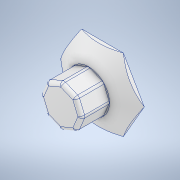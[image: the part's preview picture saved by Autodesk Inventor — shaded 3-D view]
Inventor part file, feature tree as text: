
AUTODESK INVENTOR PART (.ipt)
format: ipt  version: 2022 (Build 260153000, 153)  size: 275,456 bytes
history: native  units: in
note: dims shown in document units (in); Inventor stores cm internally (conversion verified against a paired STEP export)
features: extrude x6, sketch x6, revolve x1, shell x1, fillet x1
ambient origin geometry x8: Origin, YZ Plane, XZ Plane, XY Plane, X Axis, Y Axis, Z Axis, Center Point
bodies: Solid1 (feature_tree)
feature tree (15):
  extrude  "Extrusion1"  Depth=0.5in TaperAngle=0.0deg
  revolve  "Revolution1"  [1 undecoded]
  extrude  "Extrusion2"  Depth=3.0in TaperAngle=0.0deg
  sketch  "Sketch5"  dims[d8=0.5in d9=0.0in d11=0.05in d20=0.63in]
  extrude  "Extrusion3"  Depth=0.05in
  shell  "Shell1"  Thickness=0.63in
  extrude  "Extrusion4"  Depth=0.63in
  extrude  "Extrusion5"  Depth=0.0625in
  extrude  "Extrusion6"  Depth=0.0625in
  fillet  "Fillet2"  Radius=0.02in
  sketch  "Sketch1"  dims[d0=0.75in d1=0.5in d2=0.0in]
  sketch  "Sketch2"  dims[d3=0.25in d4=0.75in]
  sketch  "Sketch3"  dims[d5=90.0deg d6=3.0in d7=0.0in]
  sketch  "Sketch6"  dims[d21=0.04in d22=0.63in]
  sketch  "Sketch7"  dims[d23=0.04in d24=0.02in d25=0.02in d26=0.02in d27=0.02in d28=0.02in d29=0.02in d30=0.63in d31=0.04in d32=0.0in d33=0.225in d34=0.3in d35=0.5in d36=0.0in d37=0.5in d38=0.0in d39=0.5in d40=0.0in d41=0.0625in d10=0.0in d12=0.0in d13=0.0in d42=0.0344in]
note: 1 required parameter value undecoded (feature->parameter linkage not recoverable at this tier; creation-order binding heuristic only, values carry confidence <= 0.55)
